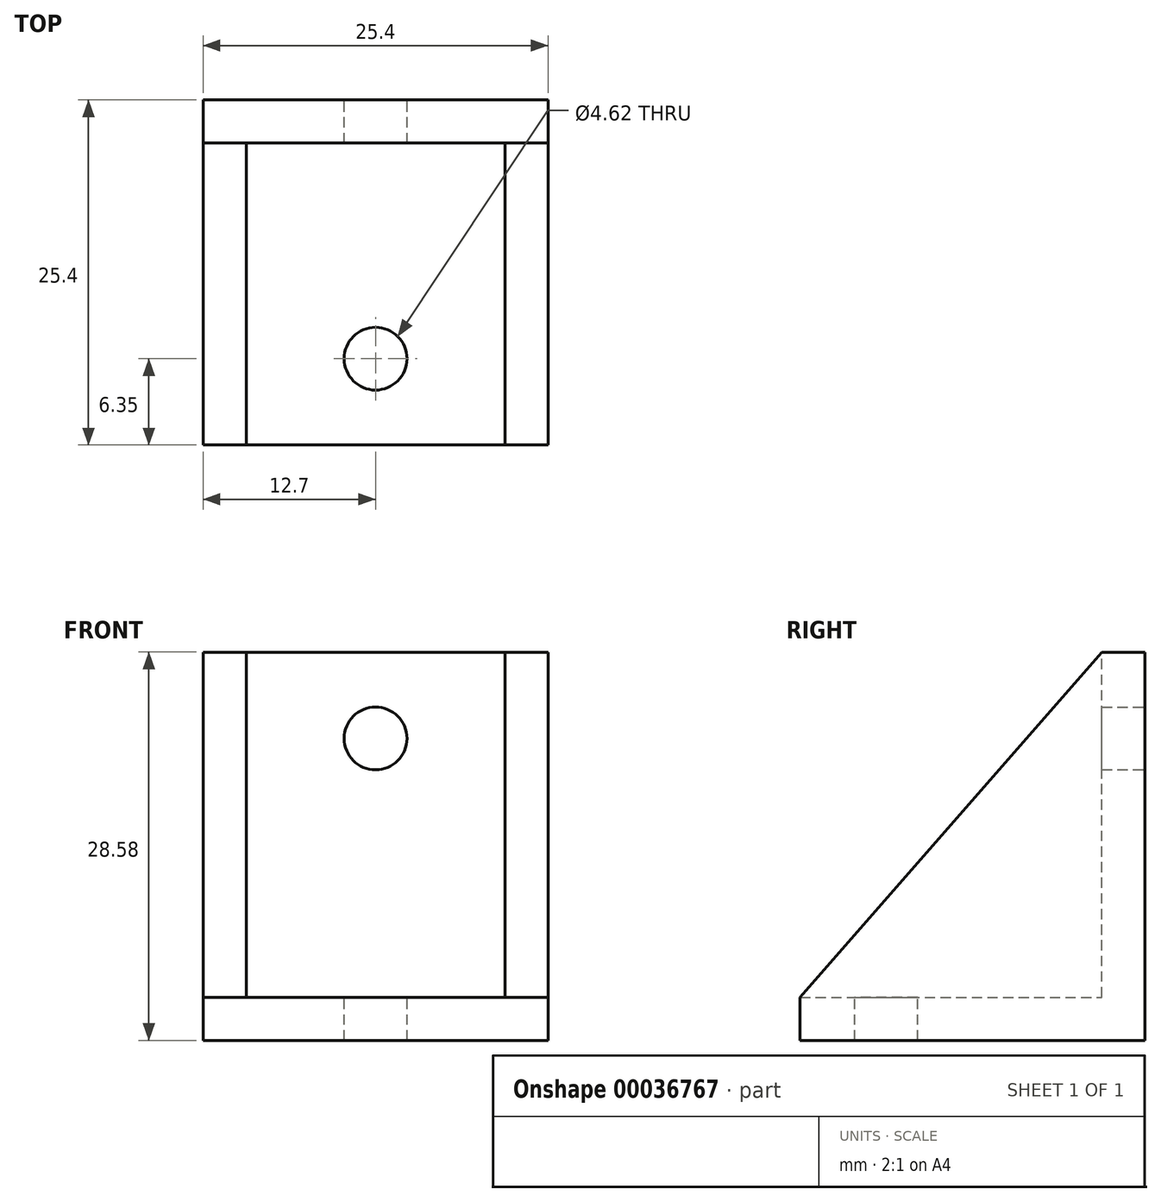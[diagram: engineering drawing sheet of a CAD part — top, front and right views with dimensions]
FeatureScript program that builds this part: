
annotation { "Feature Type Name" : "Feature", "Feature Type Description" : "" }
export const myFeature = defineFeature(function(context is Context, id is Id, definition is map)
    precondition{}
    {
        {
            var Q0;
            Q0=qCreatedBy(makeId("Front.planeOp"),FACE);
            var sketch = newSketch(context, id + "F0", { "sketchPlane" : qUnion([Q0])});
            skLineSegment(sketch, "E0.bottom", {"start": v(0, 0) * mm, "end": v(-25.4, 0) * mm});
            skLineSegment(sketch, "E0.top", {"start": v(0, 28.58) * mm, "end": v(-25.4, 28.58) * mm});
            skLineSegment(sketch, "E0.left", {"start": v(0, 0) * mm, "end": v(0, 28.58) * mm});
            skLineSegment(sketch, "E0.right", {"start": v(-25.4, 0) * mm, "end": v(-25.4, 28.58) * mm});
            skPoint(sketch, "E1.endSnap0", {"position": v(-25.4, 14.29) * mm});
            skPoint(sketch, "E2.endSnap0", {"position": v(-12.7, 0) * mm});
            skPoint(sketch, "E1.start.orphan", {"position": v(-12.7, 28.58) * mm});
            skLineSegment(sketch, "E3", {"start": v(-25.4, 0) * mm, "end": v(-25.4, 3.17) * mm});
            skLineSegment(sketch, "E4", {"start": v(-25.4, 3.17) * mm, "end": v(-25.4, 22.22) * mm});
            skLineSegment(sketch, "E5", {"start": v(-25.4, 22.22) * mm, "end": v(-12.7, 22.22) * mm});
            skCircle(sketch, "E6", {"center": v(-12.7, 22.22) * mm, "radius": 2.31 * mm});
            skSolve(sketch);
        }
        {
            var Q0;
            Q0=makeQuery(id+"F0.imprint","IMPRINT",FACE,{"disambiguationData":[TD([[makeQuery(id+"F0.imprint","IMPRINT",EDGE,{"derivedFrom":sQuery(id+"F0.wireOp",EDGE,"E0.bottom")}),-1.0]])]});
            extrude(context, id + "F1", {"entities" : qUnion([Q0]), "depth" : 3.17 * mm});
        }
        {
            var Q0;
            Q0=makeQuery(id+"F1.opExtrude","CAP_FACE",FACE,{"disambiguationData":[OSD([sQuery(id+"F0.wireOp",EDGE,"E0.bottom"),sQuery(id+"F0.wireOp",EDGE,"E0.top"),sQuery(id+"F0.wireOp",EDGE,"E0.left"),sQuery(id+"F0.wireOp",EDGE,"E0.right"),sQuery(id+"F0.wireOp",EDGE,"E3"),sQuery(id+"F0.wireOp",EDGE,"E4"),sQuery(id+"F0.wireOp",EDGE,"E6")])],"isStart":false});
            var sketch = newSketch(context, id + "F2", { "sketchPlane" : qUnion([Q0])});
            skLineSegment(sketch, "E7", {"start": v(0, 0) * mm, "end": v(0, 3.18) * mm});
            skLineSegment(sketch, "E8", {"start": v(0, 3.18) * mm, "end": v(-25.4, 3.18) * mm});
            skSolve(sketch);
        }
        {
            var Q0;
            Q0=makeQuery(id+"F2.imprint","IMPRINT",FACE,{"disambiguationData":[TD([[makeQuery(id+"F2.imprint","IMPRINT",EDGE,{"derivedFrom":sQuery(id+"F2.wireOp",EDGE,"E7")}),1.0]])]});
            extrude(context, id + "F3", {"entities" : qUnion([Q0]), "operationType" : NewBodyOperationType.ADD, "depth" : 22.22 * mm});
        }
        {
            var Q0;
            Q0=makeQuery(id+"F3.opExtrude","SWEPT_FACE",FACE,{"disambiguationData":[OSD([sQuery(id+"F2.wireOp",EDGE,"E8")])]});
            var sketch = newSketch(context, id + "F4", { "sketchPlane" : qUnion([Q0])});
            skPoint(sketch, "E9.endSnap0", {"position": v(-12.7, -25.4) * mm});
            skCircle(sketch, "E10", {"center": v(-12.7, -19.05) * mm, "radius": 2.31 * mm});
            skSolve(sketch);
        }
        {
            var Q0;
            Q0 = qSketchRegion(id + "F4", true);
            extrude(context, id + "F5", {"entities" : qUnion([Q0]), "operationType" : NewBodyOperationType.REMOVE, "oppositeDirection" : true, "depth" : 25.4 * mm});
        }
        {
            var Q0;
            Q0=makeQuery(id+"F3.boolean.opBoolean","MERGE",FACE,{"derivedFrom":[makeQuery(id+"F1.opExtrude","SWEPT_FACE",FACE,{"disambiguationData":[OSD([sQuery(id+"F0.wireOp",EDGE,"E0.left")])]}),makeQuery(id+"F3.opExtrude","SWEPT_FACE",FACE,{"disambiguationData":[OSD([sQuery(id+"F2.wireOp",EDGE,"E7")])]})]});
            var sketch = newSketch(context, id + "F6", { "sketchPlane" : qUnion([Q0])});
            skLineSegment(sketch, "E11", {"start": v(-25.4, 3.18) * mm, "end": v(-3.18, 28.58) * mm});
            skSolve(sketch);
        }
        {
            var Q0;
            Q0 = qSketchRegion(id + "F6", true);
            var Q1;
            Q1=makeQuery(id+"F6.imprint","IMPRINT",FACE,{"disambiguationData":[TD([[makeQuery(id+"F6.imprint","IMPRINT",EDGE,{"derivedFrom":sQuery(id+"F6.wireOp",EDGE,"E11")}),-1.0]])]});
            extrude(context, id + "F7", {"entities" : qUnion([Q0, Q1]), "operationType" : NewBodyOperationType.ADD, "oppositeDirection" : true, "depth" : 3.17 * mm});
        }
        {
            var Q0;
            {var subQ0=sQuery(id+"F0.wireOp",EDGE,"E0.right");var subQ1=sQuery(id+"F0.wireOp",EDGE,"E3");var subQ2=sQuery(id+"F0.wireOp",EDGE,"E4");Q0=makeQuery(id+"F3.boolean.opBoolean","MERGE",FACE,{"derivedFrom":[makeQuery(id+"F1.opExtrude","SWEPT_FACE",FACE,{"disambiguationData":[OSD([subQ0,subQ1,subQ2])]}),makeQuery(id+"F3.opExtrude","SWEPT_FACE",FACE,{"disambiguationData":[OSD([subQ0,subQ1,subQ2])]})]});}
            var sketch = newSketch(context, id + "F8", { "sketchPlane" : qUnion([Q0])});
            skLineSegment(sketch, "E12", {"start": v(25.4, 3.17) * mm, "end": v(3.17, 28.58) * mm});
            skSolve(sketch);
        }
        {
            var Q0;
            Q0=makeQuery(id+"F8.imprint","IMPRINT",FACE,{"disambiguationData":[TD([[makeQuery(id+"F8.imprint","IMPRINT",EDGE,{"derivedFrom":sQuery(id+"F8.wireOp",EDGE,"E12")}),1.0]])]});
            extrude(context, id + "F9", {"entities" : qUnion([Q0]), "operationType" : NewBodyOperationType.ADD, "oppositeDirection" : true, "depth" : 3.17 * mm});
        }
    });
